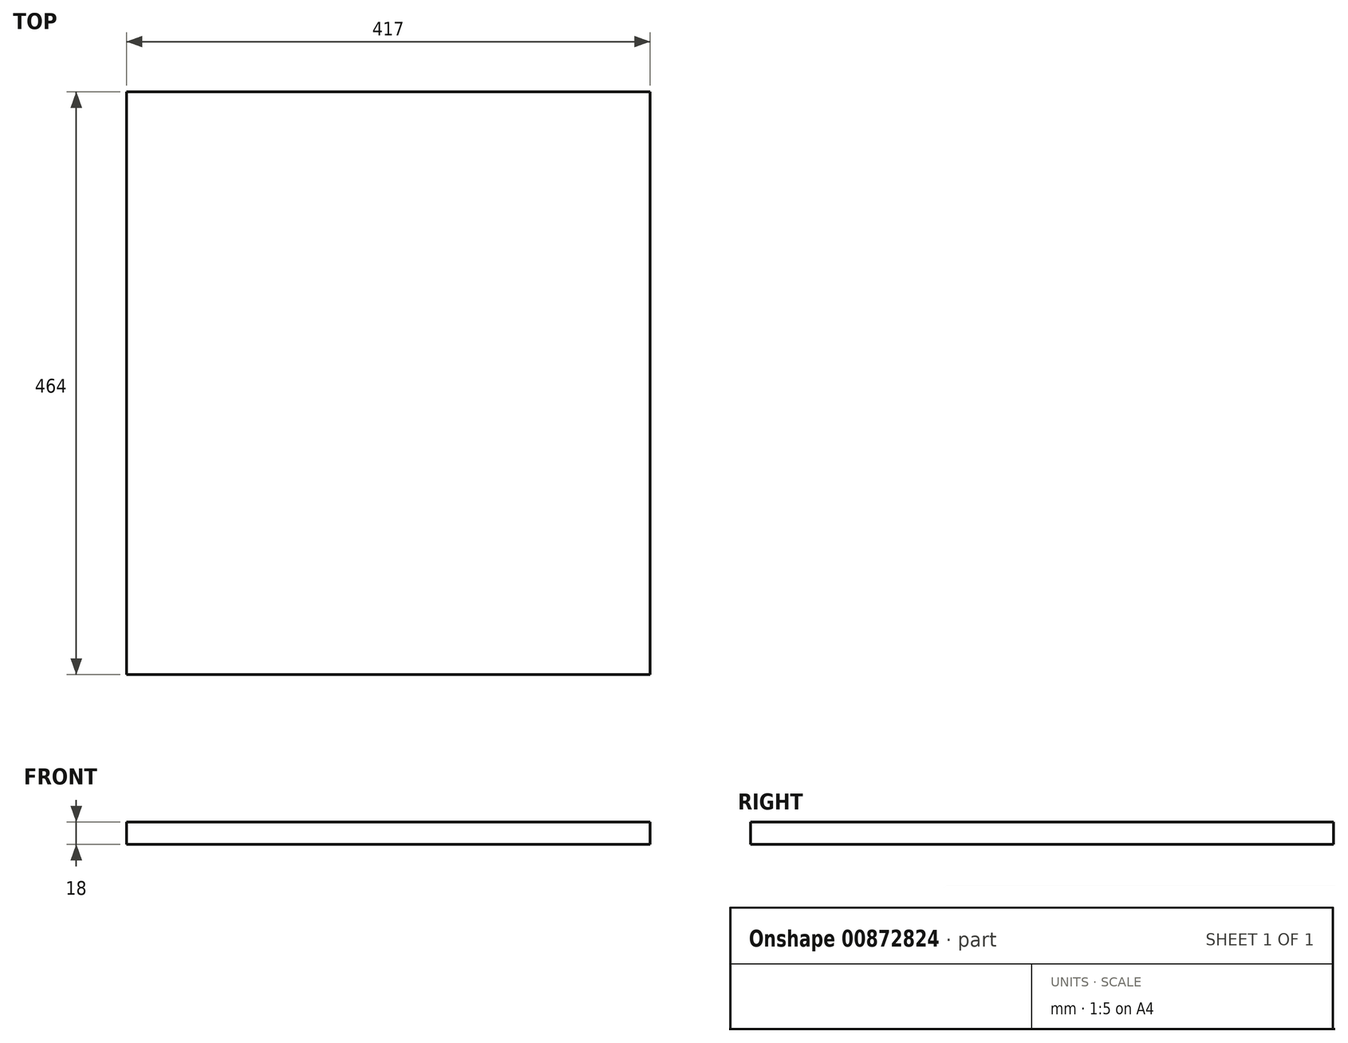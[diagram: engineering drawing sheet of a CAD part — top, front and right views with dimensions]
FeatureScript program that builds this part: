
annotation { "Feature Type Name" : "Feature", "Feature Type Description" : "" }
export const myFeature = defineFeature(function(context is Context, id is Id, definition is map)
    precondition{}
    {
        {
            var Q0;
            Q0=qCreatedBy(makeId("Top.planeOp"),FACE);
            var sketch = newSketch(context, id + "F0", { "sketchPlane" : qUnion([Q0])});
            skLineSegment(sketch, "E0.bottom", {"start": v(208.5, -231.85) * mm, "end": v(-208.5, -231.85) * mm});
            skLineSegment(sketch, "E0.top", {"start": v(208.5, 232.15) * mm, "end": v(-208.5, 232.15) * mm});
            skLineSegment(sketch, "E0.left", {"start": v(208.5, -231.85) * mm, "end": v(208.5, 232.15) * mm});
            skLineSegment(sketch, "E0.right", {"start": v(-208.5, -231.85) * mm, "end": v(-208.5, 232.15) * mm});
            skPoint(sketch, "E0.middle", {"position": v(0, 0.15) * mm});
            skSolve(sketch);
        }
        {
            var Q0;
            Q0 = qSketchRegion(id + "F0", true);
            extrude(context, id + "F1", {"entities" : qUnion([Q0]), "depth" : 18 * mm, "offsetDistance" : 25 * mm});
        }
    });
